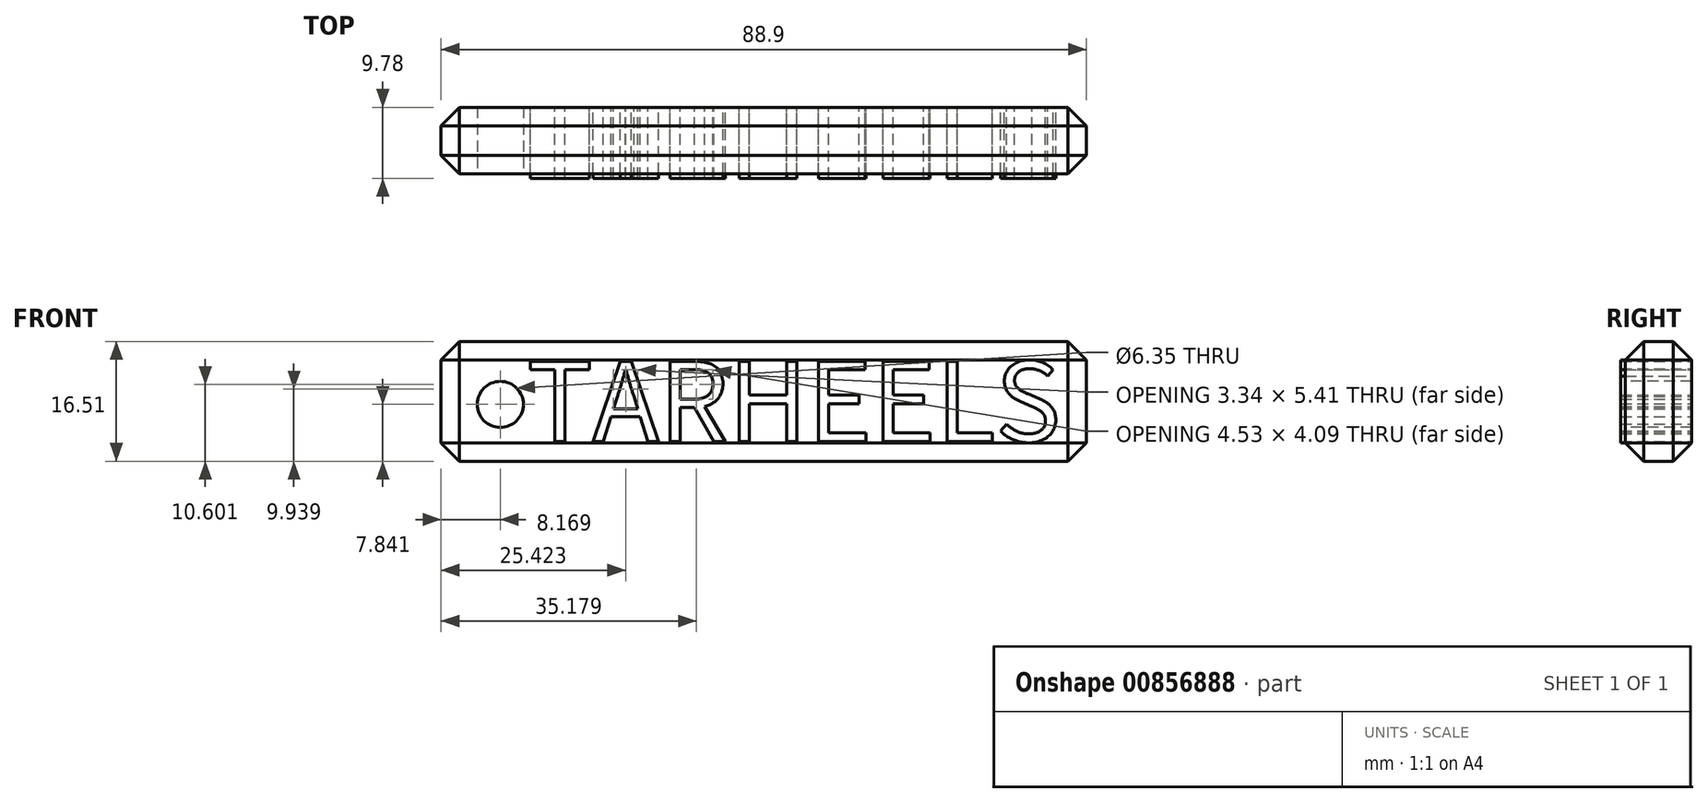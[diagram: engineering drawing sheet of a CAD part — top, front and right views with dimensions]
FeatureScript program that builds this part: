
annotation { "Feature Type Name" : "Feature", "Feature Type Description" : "" }
export const myFeature = defineFeature(function(context is Context, id is Id, definition is map)
    precondition{}
    {
        {
            var Q0;
            Q0=qCreatedBy(makeId("Front.planeOp"),FACE);
            var sketch = newSketch(context, id + "F0", { "sketchPlane" : qUnion([Q0])});
            skText(sketch, "E0", { "text": "TARHEELS", "fontName": "NotoSansCJKsc-Regular.otf"});
            const initialGuessF0  = {"E0": [-0.04002, 0.0229, 1, 0, 0.01083]};
            skSetInitialGuess(sketch, initialGuessF0);
            skSolve(sketch);
        }
        {
            var Q0;
            Q0 = qSketchRegion(id + "F0", true);
            extrude(context, id + "F1", {"entities" : qUnion([Q0]), "depth" : 9.78 * mm, "offsetDistance" : 25.4 * mm});
        }
        {
            var Q0;
            Q0=qCreatedBy(makeId("Front.planeOp"),FACE);
            var sketch = newSketch(context, id + "F2", { "sketchPlane" : qUnion([Q0])});
            skLineSegment(sketch, "E1.bottom", {"start": v(37, 36.66) * mm, "end": v(-51.9, 36.66) * mm});
            skLineSegment(sketch, "E1.top", {"start": v(37, 20.15) * mm, "end": v(-51.9, 20.15) * mm});
            skLineSegment(sketch, "E1.left", {"start": v(37, 36.66) * mm, "end": v(37, 20.15) * mm});
            skLineSegment(sketch, "E1.right", {"start": v(-51.9, 36.66) * mm, "end": v(-51.9, 20.15) * mm});
            skSolve(sketch);
        }
        {
            var Q0;
            Q0 = qSketchRegion(id + "F2", true);
            extrude(context, id + "F3", {"entities" : qUnion([Q0]), "depth" : 9.14 * mm, "offsetDistance" : 25.4 * mm});
        }
        {
            var Q0;
            Q0=makeQuery(id+"F3.opExtrude","SWEPT_FACE",FACE,{"disambiguationData":[OSD([sQuery(id+"F2.wireOp",EDGE,"E1.right")])]});
            var Q1;
            Q1=makeQuery(id+"F3.opExtrude","SWEPT_FACE",FACE,{"disambiguationData":[OSD([sQuery(id+"F2.wireOp",EDGE,"E1.bottom")])]});
            var Q2;
            Q2=makeQuery(id+"F3.opExtrude","SWEPT_FACE",FACE,{"disambiguationData":[OSD([sQuery(id+"F2.wireOp",EDGE,"E1.top")])]});
            var Q3;
            Q3=makeQuery(id+"F3.opExtrude","SWEPT_FACE",FACE,{"disambiguationData":[OSD([sQuery(id+"F2.wireOp",EDGE,"E1.left")])]});
            chamfer(context, id + "F4", {"entities" : qUnion([Q0, Q1, Q2, Q3]), "width" : 2.54 * mm, "tangentPropagation" : true});
        }
        {
            var Q0;
            Q0=makeQuery(id+"F3.opExtrude","CAP_FACE",FACE,{"disambiguationData":[OSD([sQuery(id+"F2.wireOp",EDGE,"E1.bottom"),sQuery(id+"F2.wireOp",EDGE,"E1.top"),sQuery(id+"F2.wireOp",EDGE,"E1.left"),sQuery(id+"F2.wireOp",EDGE,"E1.right")])],"isStart":false});
            var sketch = newSketch(context, id + "F5", { "sketchPlane" : qUnion([Q0])});
            skCircle(sketch, "E2", {"center": v(-43.72, 28) * mm, "radius": 3.18 * mm});
            skSolve(sketch);
        }
        {
            var Q0;
            Q0 = qSketchRegion(id + "F5", true);
            extrude(context, id + "F6", {"entities" : qUnion([Q0]), "operationType" : NewBodyOperationType.REMOVE, "oppositeDirection" : true, "depth" : 25.4 * mm, "offsetDistance" : 25.4 * mm});
        }
    });
